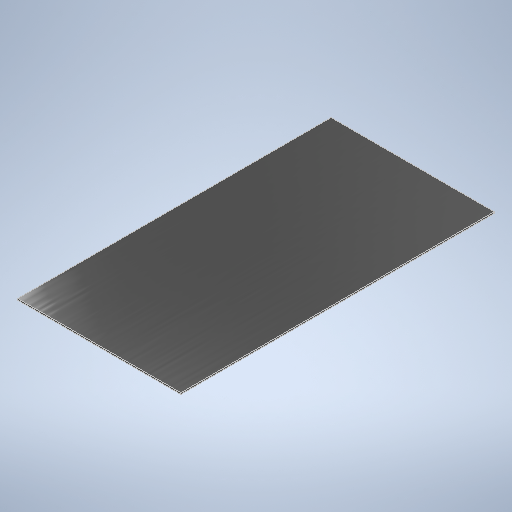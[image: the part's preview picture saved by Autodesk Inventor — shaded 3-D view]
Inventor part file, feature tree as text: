
AUTODESK INVENTOR PART (.ipt)
format: ipt  version: 2025.1 (Build 291241020, 241B)  size: 238,080 bytes
history: native  units: in
note: dims shown in document units (in); Inventor stores cm internally (conversion verified against a paired STEP export)
features: extrude x1, sketch x1
ambient origin geometry x8: Origin, YZ Plane, XZ Plane, XY Plane, X Axis, Y Axis, Z Axis, Center Point
bodies: Solid1 (feature_tree)
feature tree (2):
  extrude  "Extrusion1"  Depth=25.45in
  sketch  "Sketch1"  dims[d0=13.25in d1=25.45in d2=0.125in d3=0.0in]
